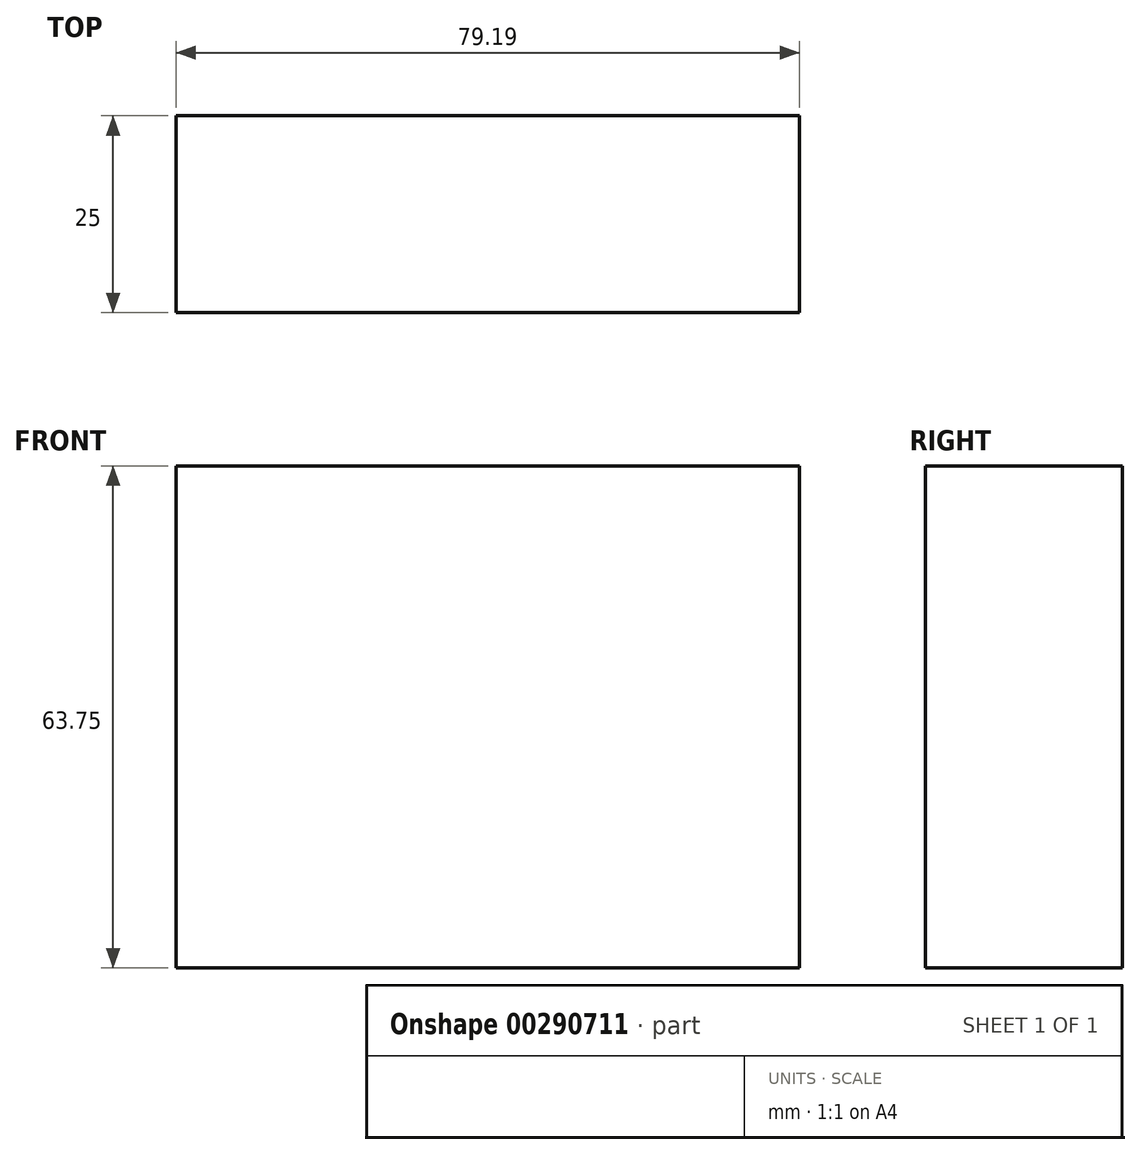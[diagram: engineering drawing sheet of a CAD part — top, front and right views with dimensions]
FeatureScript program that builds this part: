
annotation { "Feature Type Name" : "Feature", "Feature Type Description" : "" }
export const myFeature = defineFeature(function(context is Context, id is Id, definition is map)
    precondition{}
    {
        {
            var Q0;
            Q0=qCreatedBy(makeId("Front.planeOp"),FACE);
            var sketch = newSketch(context, id + "F0", { "sketchPlane" : qUnion([Q0])});
            skLineSegment(sketch, "E0.bottom", {"start": v(-92.82, 24.8) * mm, "end": v(-13.63, 24.8) * mm});
            skLineSegment(sketch, "E0.top", {"start": v(-92.82, 88.56) * mm, "end": v(-13.63, 88.56) * mm});
            skLineSegment(sketch, "E0.left", {"start": v(-92.82, 24.8) * mm, "end": v(-92.82, 88.56) * mm});
            skLineSegment(sketch, "E0.right", {"start": v(-13.63, 24.8) * mm, "end": v(-13.63, 88.56) * mm});
            skPoint(sketch, "E0.middle", {"position": v(-53.23, 56.69) * mm});
            skSolve(sketch);
        }
        {
            var Q0;
            Q0=makeQuery(id+"F0.imprint","IMPRINT",FACE,{"disambiguationData":[TD([[makeQuery(id+"F0.imprint","IMPRINT",EDGE,{"derivedFrom":sQuery(id+"F0.wireOp",EDGE,"E0.bottom")}),1.0]])]});
            extrude(context, id + "F1", {"entities" : qUnion([Q0]), "depth" : 25 * mm});
        }
    });
